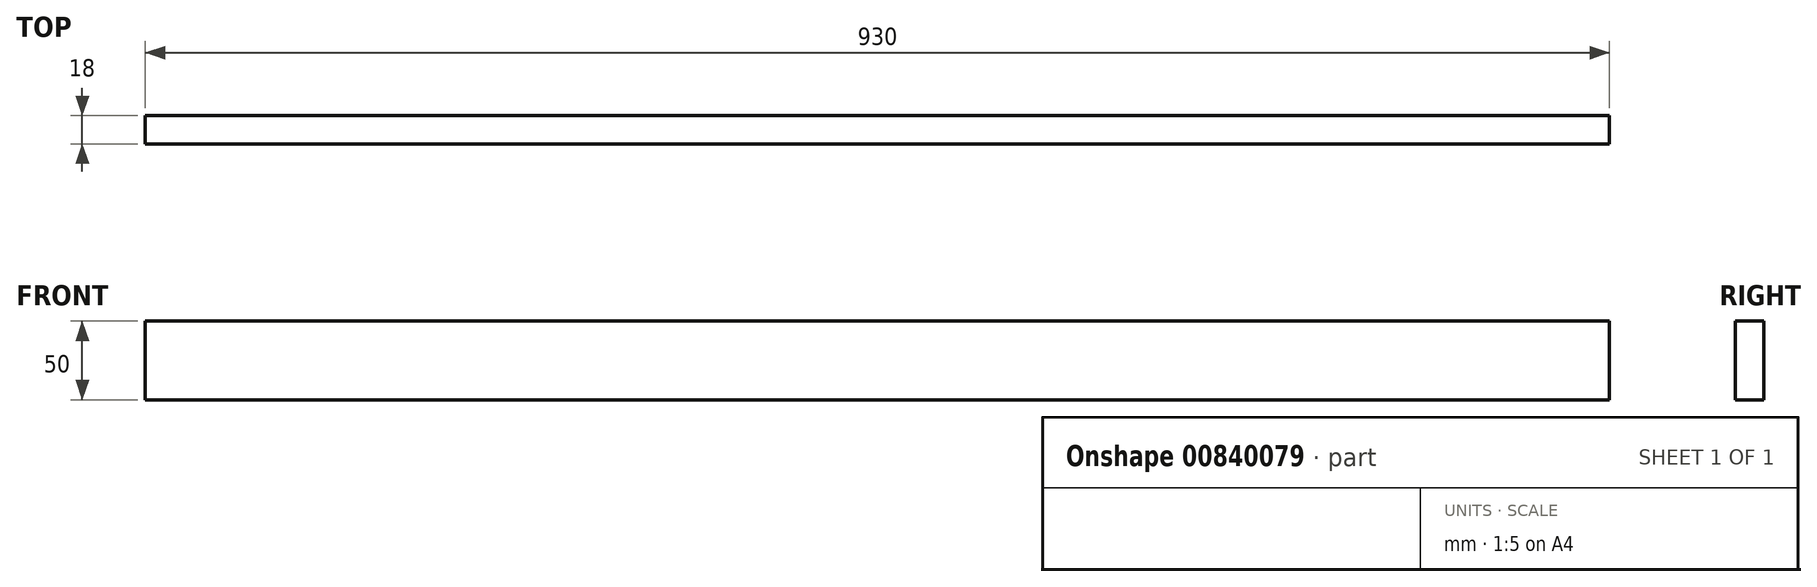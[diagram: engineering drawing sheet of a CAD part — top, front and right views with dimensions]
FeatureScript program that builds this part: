
annotation { "Feature Type Name" : "Feature", "Feature Type Description" : "" }
export const myFeature = defineFeature(function(context is Context, id is Id, definition is map)
    precondition{}
    {
        {
            var Q0;
            Q0=qCreatedBy(makeId("Front.planeOp"),FACE);
            var sketch = newSketch(context, id + "F0", { "sketchPlane" : qUnion([Q0])});
            skLineSegment(sketch, "E0.bottom", {"start": v(-465, -25) * mm, "end": v(465, -25) * mm});
            skLineSegment(sketch, "E0.top", {"start": v(-465, 25) * mm, "end": v(465, 25) * mm});
            skLineSegment(sketch, "E0.left", {"start": v(-465, -25) * mm, "end": v(-465, 25) * mm});
            skLineSegment(sketch, "E0.right", {"start": v(465, -25) * mm, "end": v(465, 25) * mm});
            skPoint(sketch, "E0.middle", {"position": v(0, 0) * mm});
            skSolve(sketch);
        }
        {
            var Q0;
            Q0=qSketchRegion(id+"F0",true);
            extrude(context, id + "F1", {"entities" : qUnion([Q0]), "depth" : 18 * mm, "offsetDistance" : 25 * mm});
        }
    });
